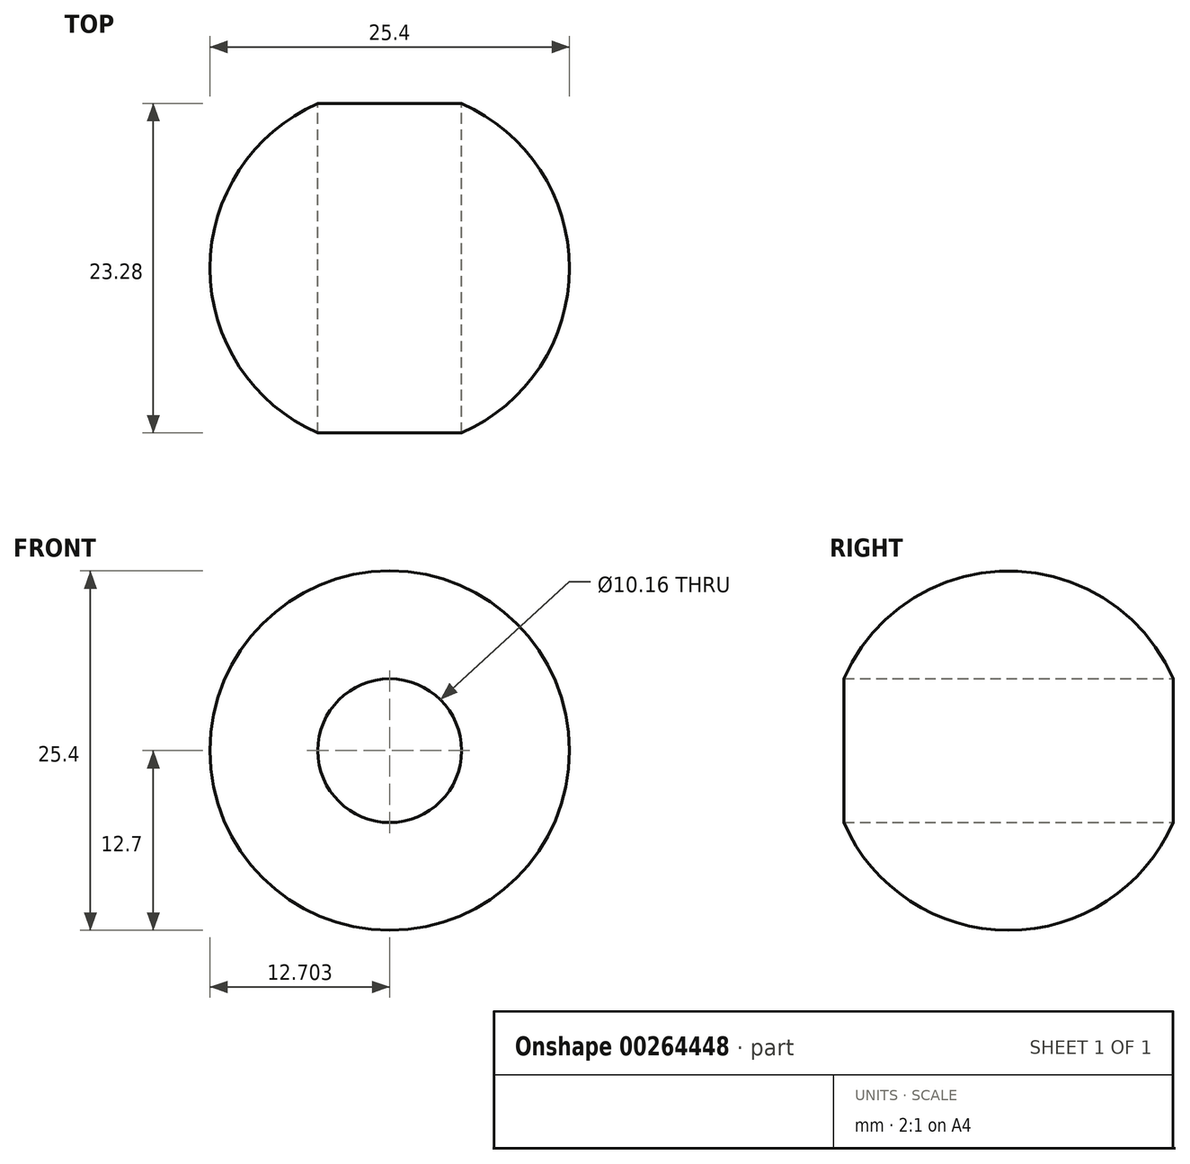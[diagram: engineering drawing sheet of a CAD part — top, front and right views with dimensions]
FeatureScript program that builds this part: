
annotation { "Feature Type Name" : "Feature", "Feature Type Description" : "" }
export const myFeature = defineFeature(function(context is Context, id is Id, definition is map)
    precondition{}
    {
        {
            var Q0;
            Q0=qCreatedBy(makeId("Top.planeOp"),FACE);
            var sketch = newSketch(context, id + "F0", { "sketchPlane" : qUnion([Q0])});
            skLineSegment(sketch, "E0", {"start": v(-31.4, 42.58) * mm, "end": v(-31.4, -46.2) * mm});
            skArc(sketch, "E1", {"start": v(-31.4, -12.7) * mm, "mid": v(-18.7, 0) * mm, "end": v(-31.4, 12.7) * mm});
            skLineSegment(sketch, "E2", {"start": v(-31.4, -12.7) * mm, "end": v(-26.32, -12.7) * mm});
            skLineSegment(sketch, "E3", {"start": v(-26.32, -12.7) * mm, "end": v(-26.32, -11.64) * mm});
            skLineSegment(sketch, "E4", {"start": v(-31.4, 12.7) * mm, "end": v(-26.32, 12.7) * mm});
            skLineSegment(sketch, "E5", {"start": v(-26.32, 12.7) * mm, "end": v(-26.32, -11.64) * mm});
            skSolve(sketch);
        }
        {
            var Q0;
            {var subQ0=sQuery(id+"F0.wireOp",EDGE,"E5");var subQ1=sQuery(id+"F0.wireOp",EDGE,"E1");var subQ3=makeQuery(id+"F0.imprint","INTERSECT",VERTEX,{"derivedFrom":[subQ1,subQ0]});Q0=makeQuery(id+"F0.imprint","IMPRINT",FACE,{"disambiguationData":[TD([[makeQuery(id+"F0.imprint","IMPRINT",EDGE,{"disambiguationData":[TD([[subQ3,1.0]])],"derivedFrom":subQ1}),1.0]])]});}
            var Q1;
            Q1=sQuery(id+"F0.wireOp",EDGE,"E0");
            revolve(context, id + "F1", {"entities" : qUnion([Q0]), "axis" : qUnion([Q1]), "revolveType" : RevolveType.FULL});
        }
    });
